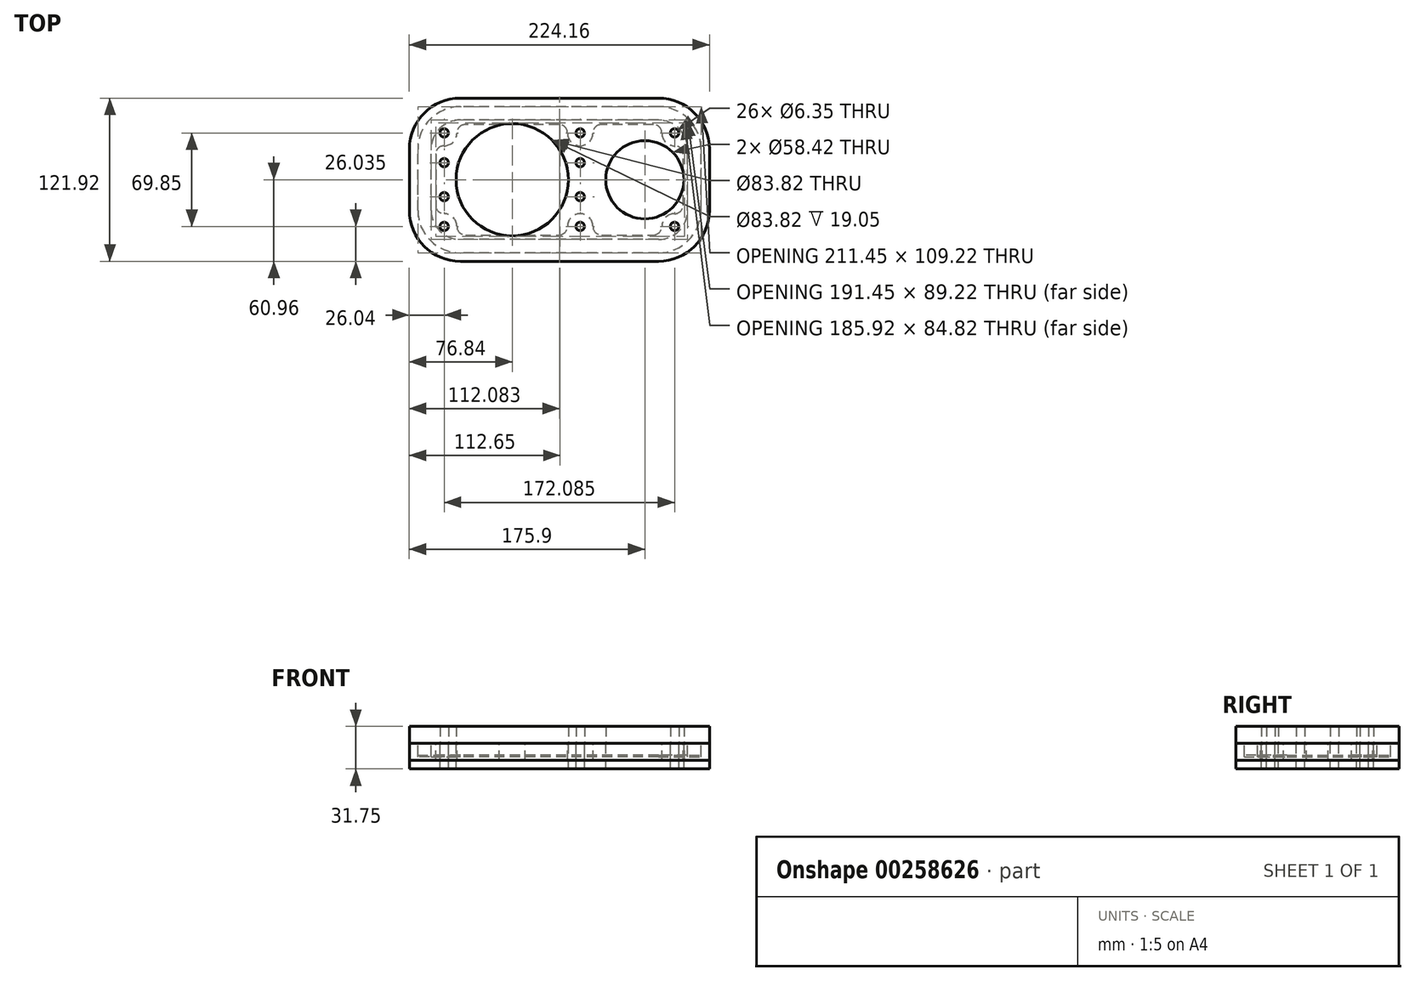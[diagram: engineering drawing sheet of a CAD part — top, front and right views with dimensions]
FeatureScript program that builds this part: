
annotation { "Feature Type Name" : "Feature", "Feature Type Description" : "" }
export const myFeature = defineFeature(function(context is Context, id is Id, definition is map)
    precondition{}
    {
        {
            var Q0;
            Q0=qCreatedBy(makeId("Top.planeOp"),FACE);
            var sketch = newSketch(context, id + "F0", { "sketchPlane" : qUnion([Q0])});
            skLineSegment(sketch, "E0.bottom", {"start": v(50.8, -12.7) * mm, "end": v(-50.8, -12.7) * mm, "construction": true});
            skLineSegment(sketch, "E0.top", {"start": v(50.8, 12.7) * mm, "end": v(-50.8, 12.7) * mm, "construction": true});
            skLineSegment(sketch, "E0.left", {"start": v(50.8, -12.7) * mm, "end": v(50.8, 12.7) * mm, "construction": true});
            skLineSegment(sketch, "E0.right", {"start": v(-50.8, -12.7) * mm, "end": v(-50.8, 12.7) * mm, "construction": true});
            skPoint(sketch, "E0.middle", {"position": v(0, 0) * mm});
            skCircle(sketch, "E1", {"center": v(0, 0) * mm, "radius": 41.91 * mm});
            skCircle(sketch, "E2", {"center": v(-50.8, 12.7) * mm, "radius": 3.18 * mm});
            skCircle(sketch, "E3", {"center": v(-50.8, -12.7) * mm, "radius": 3.18 * mm});
            skCircle(sketch, "E4", {"center": v(50.8, -12.7) * mm, "radius": 3.18 * mm});
            skCircle(sketch, "E5", {"center": v(50.8, 12.7) * mm, "radius": 3.18 * mm});
            skLineSegment(sketch, "E6.1", {"start": v(147.32, -22.86) * mm, "end": v(147.32, 22.86) * mm});
            skLineSegment(sketch, "E6.2", {"start": v(109.22, -60.96) * mm, "end": v(-38.74, -60.96) * mm});
            skLineSegment(sketch, "E6.5", {"start": v(-76.84, -22.86) * mm, "end": v(-76.84, 22.86) * mm});
            skLineSegment(sketch, "E6.7", {"start": v(109.22, 60.96) * mm, "end": v(-38.74, 60.96) * mm});
            skLineSegment(sketch, "E7", {"start": v(0, 0) * mm, "end": v(99.06, 0) * mm});
            skCircle(sketch, "E8", {"center": v(99.06, 0) * mm, "radius": 29.21 * mm});
            skPoint(sketch, "E9.visualSharp", {"position": v(-76.84, 60.96) * mm});
            skArc(sketch, "E9.filletArc", {"start": v(-38.74, 60.96) * mm, "mid": v(-65.68, 49.8) * mm, "end": v(-76.84, 22.86) * mm});
            skPoint(sketch, "E10.visualSharp", {"position": v(-76.84, -60.96) * mm});
            skArc(sketch, "E10.filletArc", {"start": v(-76.84, -22.86) * mm, "mid": v(-65.68, -49.8) * mm, "end": v(-38.74, -60.96) * mm});
            skPoint(sketch, "E11.visualSharp", {"position": v(147.32, -60.96) * mm});
            skArc(sketch, "E11.filletArc", {"start": v(109.22, -60.96) * mm, "mid": v(136.16, -49.8) * mm, "end": v(147.32, -22.86) * mm});
            skPoint(sketch, "E12.visualSharp", {"position": v(147.32, 60.96) * mm});
            skArc(sketch, "E12.filletArc", {"start": v(147.32, 22.86) * mm, "mid": v(136.16, 49.8) * mm, "end": v(109.22, 60.96) * mm});
            skArc(sketch, "E13.0", {"start": v(109.22, -54.61) * mm, "mid": v(131.67, -45.31) * mm, "end": v(140.97, -22.86) * mm});
            skLineSegment(sketch, "E13.1", {"start": v(140.97, -22.86) * mm, "end": v(140.97, 22.86) * mm});
            skLineSegment(sketch, "E13.2", {"start": v(109.22, -54.6) * mm, "end": v(-38.74, -54.61) * mm});
            skArc(sketch, "E13.3", {"start": v(140.97, 22.86) * mm, "mid": v(131.67, 45.31) * mm, "end": v(109.22, 54.61) * mm});
            skArc(sketch, "E13.4", {"start": v(-70.49, -22.86) * mm, "mid": v(-61.19, -45.31) * mm, "end": v(-38.74, -54.6) * mm});
            skLineSegment(sketch, "E13.5", {"start": v(-70.49, -22.86) * mm, "end": v(-70.49, 22.86) * mm});
            skArc(sketch, "E13.6", {"start": v(-38.74, 54.6) * mm, "mid": v(-61.19, 45.31) * mm, "end": v(-70.49, 22.86) * mm});
            skLineSegment(sketch, "E13.7", {"start": v(109.22, 54.61) * mm, "end": v(-38.74, 54.6) * mm});
            skArc(sketch, "E14.0", {"start": v(109.22, -44.61) * mm, "mid": v(124.6, -38.24) * mm, "end": v(130.97, -22.86) * mm});
            skLineSegment(sketch, "E14.1", {"start": v(130.97, -22.86) * mm, "end": v(130.97, 22.86) * mm});
            skLineSegment(sketch, "E14.2", {"start": v(109.22, -44.6) * mm, "end": v(-38.74, -44.61) * mm});
            skArc(sketch, "E14.3", {"start": v(130.97, 22.86) * mm, "mid": v(124.6, 38.24) * mm, "end": v(109.22, 44.61) * mm});
            skArc(sketch, "E14.4", {"start": v(-60.49, -22.86) * mm, "mid": v(-54.11, -38.24) * mm, "end": v(-38.74, -44.6) * mm});
            skLineSegment(sketch, "E14.5", {"start": v(-60.49, -22.86) * mm, "end": v(-60.49, 22.86) * mm});
            skArc(sketch, "E14.6", {"start": v(-38.74, 44.6) * mm, "mid": v(-54.11, 38.24) * mm, "end": v(-60.49, 22.86) * mm});
            skLineSegment(sketch, "E14.7", {"start": v(109.22, 44.61) * mm, "end": v(-38.74, 44.6) * mm});
            skCircle(sketch, "E15", {"center": v(-50.8, 34.93) * mm, "radius": 3.18 * mm});
            skCircle(sketch, "E16", {"center": v(50.8, 34.93) * mm, "radius": 3.18 * mm});
            skCircle(sketch, "E17", {"center": v(121.29, 34.93) * mm, "radius": 3.18 * mm});
            skCircle(sketch, "E18", {"center": v(121.29, -34.93) * mm, "radius": 3.18 * mm});
            skCircle(sketch, "E19", {"center": v(50.8, -34.93) * mm, "radius": 3.18 * mm});
            skCircle(sketch, "E20", {"center": v(-50.8, -34.93) * mm, "radius": 3.18 * mm});
            skLineSegment(sketch, "E21", {"start": v(0, 41.91) * mm, "end": v(0, 60.96) * mm, "construction": true});
            skLineSegment(sketch, "E22", {"start": v(128.27, 0) * mm, "end": v(147.32, 0) * mm, "construction": true});
            skLineSegment(sketch, "E23", {"start": v(0, -41.91) * mm, "end": v(0, -60.96) * mm, "construction": true});
            skPoint(sketch, "E24", {"position": v(41.91, 0) * mm});
            skPoint(sketch, "E25", {"position": v(69.85, 0) * mm});
            skSolve(sketch);
        }
        {
            var Q0;
            Q0=makeQuery(id+"F0.imprint","IMPRINT",FACE,{"disambiguationData":[TD([[makeQuery(id+"F0.imprint","IMPRINT",EDGE,{"derivedFrom":sQuery(id+"F0.wireOp",EDGE,"E1")}),-1.0]])]});
            var Q1;
            Q1=makeQuery(id+"F0.imprint","IMPRINT",FACE,{"disambiguationData":[TD([[makeQuery(id+"F0.imprint","IMPRINT",EDGE,{"derivedFrom":sQuery(id+"F0.wireOp",EDGE,"E13.0")}),1.0]])]});
            var Q2;
            Q2=makeQuery(id+"F0.imprint","IMPRINT",FACE,{"disambiguationData":[TD([[makeQuery(id+"F0.imprint","IMPRINT",EDGE,{"derivedFrom":sQuery(id+"F0.wireOp",EDGE,"E6.1")}),1.0]])]});
            extrude(context, id + "F1", {"entities" : qUnion([Q0, Q1, Q2]), "oppositeDirection" : true, "depth" : 19.05 * mm});
        }
        {
            var Q0;
            Q0=makeQuery(id+"F0.imprint","IMPRINT",FACE,{"disambiguationData":[TD([[makeQuery(id+"F0.imprint","IMPRINT",EDGE,{"derivedFrom":sQuery(id+"F0.wireOp",EDGE,"E13.0")}),1.0]])]});
            extrude(context, id + "F2", {"entities" : qUnion([Q0]), "operationType" : NewBodyOperationType.REMOVE, "oppositeDirection" : true, "depth" : 10 * mm});
        }
        {
            var Q0;
            Q0=qCreatedBy(makeId("Top.planeOp"),FACE);
            var sketch = newSketch(context, id + "F3", { "sketchPlane" : qUnion([Q0])});
            skPoint(sketch, "E26.0", {"position": v(-50.8, 34.93) * mm});
            skPoint(sketch, "E27.0", {"position": v(-50.8, -34.93) * mm});
            skPoint(sketch, "E28.0", {"position": v(-50.8, 12.7) * mm});
            skPoint(sketch, "E29.0", {"position": v(-50.8, -12.7) * mm});
            skPoint(sketch, "E30.0", {"position": v(0, 0) * mm});
            skPoint(sketch, "E31.0", {"position": v(50.8, 34.93) * mm});
            skPoint(sketch, "E32.0", {"position": v(50.8, 12.7) * mm});
            skPoint(sketch, "E33.0", {"position": v(50.8, -12.7) * mm});
            skPoint(sketch, "E34.0", {"position": v(50.8, -34.93) * mm});
            skPoint(sketch, "E35.0", {"position": v(99.06, 0) * mm});
            skPoint(sketch, "E36.0", {"position": v(121.29, 34.93) * mm});
            skPoint(sketch, "E37.0", {"position": v(121.29, -34.93) * mm});
            skPoint(sketch, "E38.0", {"position": v(109.22, -22.86) * mm});
            skPoint(sketch, "E39.0", {"position": v(109.22, -60.96) * mm});
            skPoint(sketch, "E40.0", {"position": v(147.32, -22.86) * mm});
            skPoint(sketch, "E41.0", {"position": v(147.32, 22.86) * mm});
            skPoint(sketch, "E42.0", {"position": v(109.22, 60.96) * mm});
            skPoint(sketch, "E43.0", {"position": v(-38.74, 60.96) * mm});
            skPoint(sketch, "E44.0", {"position": v(-76.84, 22.86) * mm});
            skPoint(sketch, "E45.0", {"position": v(-76.84, -22.86) * mm});
            skPoint(sketch, "E46.0", {"position": v(-38.74, -60.96) * mm});
            skPoint(sketch, "E47.0", {"position": v(-38.74, 22.86) * mm});
            skPoint(sketch, "E48.0", {"position": v(-38.74, -22.86) * mm});
            skArc(sketch, "E49", {"start": v(-38.74, 60.96) * mm, "mid": v(-65.68, 49.8) * mm, "end": v(-76.84, 22.86) * mm});
            skArc(sketch, "E50", {"start": v(-76.84, -22.86) * mm, "mid": v(-65.68, -49.8) * mm, "end": v(-38.74, -60.96) * mm});
            skArc(sketch, "E51", {"start": v(109.22, -60.96) * mm, "mid": v(136.16, -49.8) * mm, "end": v(147.32, -22.86) * mm});
            skPoint(sketch, "E52.0", {"position": v(109.22, 22.86) * mm});
            skArc(sketch, "E53", {"start": v(147.32, 22.86) * mm, "mid": v(136.16, 49.8) * mm, "end": v(109.22, 60.96) * mm});
            skLineSegment(sketch, "E54", {"start": v(-38.74, 60.96) * mm, "end": v(109.22, 60.96) * mm});
            skLineSegment(sketch, "E55", {"start": v(147.32, 22.86) * mm, "end": v(147.32, -22.86) * mm});
            skLineSegment(sketch, "E56", {"start": v(109.22, -60.96) * mm, "end": v(-38.74, -60.96) * mm});
            skLineSegment(sketch, "E57", {"start": v(-76.84, -22.86) * mm, "end": v(-76.84, 22.86) * mm});
            skPoint(sketch, "E58.0", {"position": v(41.91, 0) * mm});
            skPoint(sketch, "E59.0", {"position": v(69.85, 0) * mm});
            skCircle(sketch, "E60", {"center": v(0, 0) * mm, "radius": 41.91 * mm});
            skCircle(sketch, "E61", {"center": v(99.06, 0) * mm, "radius": 29.21 * mm});
            skCircle(sketch, "E62", {"center": v(-50.8, 34.93) * mm, "radius": 3.18 * mm});
            skCircle(sketch, "E63", {"center": v(-50.8, 12.7) * mm, "radius": 3.18 * mm});
            skCircle(sketch, "E64", {"center": v(-50.8, -12.7) * mm, "radius": 3.17 * mm});
            skCircle(sketch, "E65", {"center": v(-50.8, -34.93) * mm, "radius": 3.17 * mm});
            skCircle(sketch, "E66", {"center": v(50.8, -34.93) * mm, "radius": 3.18 * mm});
            skCircle(sketch, "E67", {"center": v(50.8, -12.7) * mm, "radius": 3.18 * mm});
            skCircle(sketch, "E68", {"center": v(50.8, 12.7) * mm, "radius": 3.18 * mm});
            skCircle(sketch, "E69", {"center": v(50.8, 34.93) * mm, "radius": 3.18 * mm});
            skCircle(sketch, "E70", {"center": v(121.29, 34.93) * mm, "radius": 3.18 * mm});
            skCircle(sketch, "E71", {"center": v(121.29, -34.93) * mm, "radius": 3.18 * mm});
            skSolve(sketch);
        }
        {
            var Q0;
            Q0=qCreatedBy(makeId("Top.planeOp"),FACE);
            var sketch = newSketch(context, id + "F4", { "sketchPlane" : qUnion([Q0])});
            skPoint(sketch, "E72.0", {"position": v(-38.74, 22.86) * mm});
            skPoint(sketch, "E73.0", {"position": v(-38.74, -22.86) * mm});
            skPoint(sketch, "E74.0", {"position": v(-38.74, -60.96) * mm});
            skPoint(sketch, "E75.0", {"position": v(-38.74, -54.61) * mm});
            skPoint(sketch, "E76.0", {"position": v(-38.74, -44.61) * mm});
            skPoint(sketch, "E77.0", {"position": v(-60.49, -22.86) * mm});
            skPoint(sketch, "E78.0", {"position": v(-70.49, -22.86) * mm});
            skPoint(sketch, "E79.0", {"position": v(-76.84, -22.86) * mm});
            skPoint(sketch, "E80.0", {"position": v(-76.84, 22.86) * mm});
            skPoint(sketch, "E81.0", {"position": v(-70.49, 22.86) * mm});
            skPoint(sketch, "E82.0", {"position": v(-60.49, 22.86) * mm});
            skPoint(sketch, "E83.0", {"position": v(-38.74, 44.6) * mm});
            skPoint(sketch, "E84.0", {"position": v(-38.74, 54.6) * mm});
            skPoint(sketch, "E85.0", {"position": v(-38.74, 60.96) * mm});
            skPoint(sketch, "E86.0", {"position": v(109.22, 60.96) * mm});
            skPoint(sketch, "E87.0", {"position": v(109.22, 54.61) * mm});
            skPoint(sketch, "E88.0", {"position": v(109.22, 44.61) * mm});
            skPoint(sketch, "E89.0", {"position": v(109.22, 22.86) * mm});
            skPoint(sketch, "E90.0", {"position": v(130.97, 22.86) * mm});
            skPoint(sketch, "E91.0", {"position": v(140.97, 22.86) * mm});
            skPoint(sketch, "E92.0", {"position": v(147.32, 22.86) * mm});
            skPoint(sketch, "E93.0", {"position": v(147.32, -22.86) * mm});
            skPoint(sketch, "E94.0", {"position": v(140.97, -22.86) * mm});
            skPoint(sketch, "E95.0", {"position": v(130.97, -22.86) * mm});
            skPoint(sketch, "E96.0", {"position": v(109.22, -44.6) * mm});
            skPoint(sketch, "E97.0", {"position": v(109.22, -54.6) * mm});
            skPoint(sketch, "E98.0", {"position": v(109.22, -60.96) * mm});
            skPoint(sketch, "E99.0", {"position": v(-50.8, 34.93) * mm});
            skPoint(sketch, "E100.0", {"position": v(-50.8, -34.93) * mm});
            skPoint(sketch, "E101.0", {"position": v(50.8, -34.93) * mm});
            skPoint(sketch, "E102.0", {"position": v(50.8, 34.93) * mm});
            skPoint(sketch, "E103.0", {"position": v(121.29, 34.93) * mm});
            skPoint(sketch, "E104.0", {"position": v(121.29, -34.93) * mm});
            skArc(sketch, "E105", {"start": v(-38.74, 44.6) * mm, "mid": v(-54.11, 38.24) * mm, "end": v(-60.49, 22.86) * mm});
            skArc(sketch, "E106", {"start": v(-38.74, 54.61) * mm, "mid": v(-61.19, 45.31) * mm, "end": v(-70.49, 22.86) * mm});
            skArc(sketch, "E107", {"start": v(-38.74, 60.96) * mm, "mid": v(-65.68, 49.8) * mm, "end": v(-76.84, 22.86) * mm});
            skArc(sketch, "E108", {"start": v(-60.49, -22.86) * mm, "mid": v(-54.11, -38.24) * mm, "end": v(-38.74, -44.6) * mm});
            skArc(sketch, "E109", {"start": v(-70.48, -22.86) * mm, "mid": v(-61.19, -45.31) * mm, "end": v(-38.74, -54.6) * mm});
            skArc(sketch, "E110", {"start": v(-76.84, -22.86) * mm, "mid": v(-65.68, -49.8) * mm, "end": v(-38.74, -60.96) * mm});
            skPoint(sketch, "E111.0", {"position": v(109.22, -22.86) * mm});
            skArc(sketch, "E112", {"start": v(130.97, -22.86) * mm, "mid": v(124.6, -38.24) * mm, "end": v(109.22, -44.61) * mm});
            skArc(sketch, "E113", {"start": v(140.97, -22.86) * mm, "mid": v(131.67, -45.31) * mm, "end": v(109.22, -54.61) * mm});
            skArc(sketch, "E114", {"start": v(147.32, -22.86) * mm, "mid": v(136.16, -49.8) * mm, "end": v(109.22, -60.96) * mm});
            skArc(sketch, "E115", {"start": v(130.97, 22.86) * mm, "mid": v(124.6, 38.24) * mm, "end": v(109.22, 44.61) * mm});
            skArc(sketch, "E116", {"start": v(140.97, 22.86) * mm, "mid": v(131.67, 45.31) * mm, "end": v(109.22, 54.61) * mm});
            skArc(sketch, "E117", {"start": v(147.32, 22.86) * mm, "mid": v(136.16, 49.8) * mm, "end": v(109.22, 60.96) * mm});
            skLineSegment(sketch, "E118", {"start": v(109.22, 44.61) * mm, "end": v(-38.74, 44.6) * mm});
            skLineSegment(sketch, "E119", {"start": v(-38.74, 54.6) * mm, "end": v(109.22, 54.61) * mm});
            skLineSegment(sketch, "E120", {"start": v(109.22, 60.96) * mm, "end": v(-38.74, 60.96) * mm});
            skLineSegment(sketch, "E121", {"start": v(-60.49, 22.86) * mm, "end": v(-60.49, -22.86) * mm});
            skLineSegment(sketch, "E122", {"start": v(-70.49, -22.86) * mm, "end": v(-70.49, 22.86) * mm});
            skLineSegment(sketch, "E123", {"start": v(-76.84, 22.86) * mm, "end": v(-76.84, -22.86) * mm});
            skLineSegment(sketch, "E124", {"start": v(-38.74, -44.61) * mm, "end": v(109.22, -44.6) * mm});
            skLineSegment(sketch, "E125", {"start": v(109.22, -54.6) * mm, "end": v(-38.74, -54.6) * mm});
            skLineSegment(sketch, "E126", {"start": v(-38.74, -60.96) * mm, "end": v(109.22, -60.96) * mm});
            skLineSegment(sketch, "E127", {"start": v(130.97, -22.86) * mm, "end": v(130.97, 22.86) * mm});
            skLineSegment(sketch, "E128", {"start": v(140.97, -22.86) * mm, "end": v(140.97, 22.86) * mm});
            skLineSegment(sketch, "E129", {"start": v(147.32, -22.86) * mm, "end": v(147.32, 22.86) * mm});
            skPoint(sketch, "E130.0", {"position": v(-50.8, -12.7) * mm});
            skPoint(sketch, "E131.0", {"position": v(-50.8, 12.7) * mm});
            skPoint(sketch, "E132.0", {"position": v(50.8, -12.7) * mm});
            skPoint(sketch, "E133.0", {"position": v(50.8, 12.7) * mm});
            skArc(sketch, "E134", {"start": v(-50.8, 25.4) * mm, "mid": v(-44.06, 28.19) * mm, "end": v(-41.28, 34.93) * mm});
            skArc(sketch, "E135", {"start": v(-50.8, 25.4) * mm, "mid": v(-55.3, 23.54) * mm, "end": v(-57.15, 19.05) * mm});
            skArc(sketch, "E136", {"start": v(-41.28, -34.93) * mm, "mid": v(-44.06, -28.19) * mm, "end": v(-50.8, -25.4) * mm});
            skArc(sketch, "E137", {"start": v(-41.28, -34.93) * mm, "mid": v(-39.42, -39.42) * mm, "end": v(-34.93, -41.28) * mm});
            skArc(sketch, "E138", {"start": v(34.93, -41.28) * mm, "mid": v(39.42, -39.42) * mm, "end": v(41.28, -34.93) * mm});
            skArc(sketch, "E139", {"start": v(60.33, -34.93) * mm, "mid": v(50.8, -25.4) * mm, "end": v(41.28, -34.93) * mm});
            skArc(sketch, "E140", {"start": v(60.33, -34.93) * mm, "mid": v(62.18, -39.42) * mm, "end": v(66.68, -41.28) * mm});
            skArc(sketch, "E141", {"start": v(105.41, -41.27) * mm, "mid": v(109.9, -39.42) * mm, "end": v(111.76, -34.92) * mm});
            skArc(sketch, "E142", {"start": v(121.29, -25.4) * mm, "mid": v(114.55, -28.19) * mm, "end": v(111.76, -34.92) * mm});
            skArc(sketch, "E143", {"start": v(121.29, -25.4) * mm, "mid": v(125.78, -23.54) * mm, "end": v(127.64, -19.05) * mm});
            skArc(sketch, "E144", {"start": v(127.64, 19.05) * mm, "mid": v(125.78, 23.54) * mm, "end": v(121.29, 25.4) * mm});
            skArc(sketch, "E145", {"start": v(111.76, 34.93) * mm, "mid": v(114.55, 28.19) * mm, "end": v(121.29, 25.4) * mm});
            skArc(sketch, "E146", {"start": v(111.76, 34.93) * mm, "mid": v(109.9, 39.42) * mm, "end": v(105.41, 41.28) * mm});
            skArc(sketch, "E147", {"start": v(66.68, 41.28) * mm, "mid": v(62.18, 39.42) * mm, "end": v(60.33, 34.93) * mm});
            skArc(sketch, "E148", {"start": v(-34.93, 41.28) * mm, "mid": v(-39.42, 39.42) * mm, "end": v(-41.28, 34.93) * mm});
            skArc(sketch, "E149", {"start": v(41.28, 34.93) * mm, "mid": v(50.8, 25.4) * mm, "end": v(60.33, 34.93) * mm});
            skArc(sketch, "E150", {"start": v(41.28, 34.93) * mm, "mid": v(39.42, 39.42) * mm, "end": v(34.93, 41.28) * mm});
            skArc(sketch, "E151", {"start": v(-57.15, -19.05) * mm, "mid": v(-55.3, -23.54) * mm, "end": v(-50.8, -25.4) * mm});
            skLineSegment(sketch, "E152", {"start": v(-57.15, 19.05) * mm, "end": v(-57.15, -19.05) * mm});
            skLineSegment(sketch, "E153", {"start": v(-34.93, -41.28) * mm, "end": v(-9.75, -41.28) * mm});
            skLineSegment(sketch, "E154", {"start": v(66.68, -41.28) * mm, "end": v(105.41, -41.28) * mm});
            skLineSegment(sketch, "E155", {"start": v(127.64, -19.05) * mm, "end": v(127.64, -8.13) * mm});
            skLineSegment(sketch, "E156", {"start": v(105.41, 41.28) * mm, "end": v(66.68, 41.28) * mm});
            skLineSegment(sketch, "E157", {"start": v(34.93, 41.28) * mm, "end": v(9.75, 41.28) * mm});
            skCircle(sketch, "E158", {"center": v(-50.8, 34.93) * mm, "radius": 3.18 * mm});
            skCircle(sketch, "E159", {"center": v(-50.8, -34.93) * mm, "radius": 3.18 * mm});
            skCircle(sketch, "E160", {"center": v(50.8, -34.93) * mm, "radius": 3.18 * mm});
            skCircle(sketch, "E161", {"center": v(50.8, 34.93) * mm, "radius": 3.18 * mm});
            skCircle(sketch, "E162", {"center": v(121.29, 34.93) * mm, "radius": 3.18 * mm});
            skCircle(sketch, "E163", {"center": v(121.29, -34.93) * mm, "radius": 3.18 * mm});
            skCircle(sketch, "E164.0", {"center": v(99.06, 0) * mm, "radius": 29.21 * mm});
            skPoint(sketch, "E165.0", {"position": v(0, 0) * mm});
            skCircle(sketch, "E166.0", {"center": v(0, 0) * mm, "radius": 41.91 * mm});
            skArc(sketch, "E167", {"start": v(-9.75, -41.28) * mm, "mid": v(0, -42.41) * mm, "end": v(9.75, -41.28) * mm});
            skArc(sketch, "E168", {"start": v(127.64, -8.13) * mm, "mid": v(128.77, 0) * mm, "end": v(127.64, 8.13) * mm});
            skArc(sketch, "E169.trimOffspring", {"start": v(9.75, 41.28) * mm, "mid": v(0, 42.41) * mm, "end": v(-9.75, 41.28) * mm});
            skLineSegment(sketch, "E170", {"start": v(-9.75, 41.28) * mm, "end": v(-34.93, 41.28) * mm});
            skLineSegment(sketch, "E171", {"start": v(9.75, 41.28) * mm, "end": v(-9.75, 41.28) * mm, "construction": true});
            skLineSegment(sketch, "E172", {"start": v(-9.75, -41.28) * mm, "end": v(9.75, -41.28) * mm, "construction": true});
            skLineSegment(sketch, "E173", {"start": v(9.75, -41.28) * mm, "end": v(34.93, -41.28) * mm});
            skLineSegment(sketch, "E174", {"start": v(127.64, 8.13) * mm, "end": v(127.64, 19.05) * mm});
            skLineSegment(sketch, "E175", {"start": v(127.64, -8.13) * mm, "end": v(127.64, 8.13) * mm, "construction": true});
            skSolve(sketch);
        }
        {
            var Q0;
            Q0 = qSketchRegion(id + "F3", true);
            extrude(context, id + "F5", {"entities" : qUnion([Q0]), "depth" : 12.7 * mm});
        }
        {
            var Q0;
            Q0 = qSketchRegion(id + "F4", true);
            var Q1;
            Q1=makeQuery(id+"F4.imprint","IMPRINT",FACE,{"disambiguationData":[TD([[makeQuery(id+"F4.imprint","IMPRINT",EDGE,{"derivedFrom":sQuery(id+"F4.wireOp",EDGE,"E105")}),-1.0]])]});
            var Q2;
            Q2=makeQuery(id+"F4.imprint","IMPRINT",FACE,{"disambiguationData":[TD([[makeQuery(id+"F4.imprint","IMPRINT",EDGE,{"derivedFrom":sQuery(id+"F4.wireOp",EDGE,"E105")}),1.0]])]});
            extrude(context, id + "F6", {"entities" : qUnion([Q0, Q1, Q2]), "oppositeDirection" : true, "depth" : 12.7 * mm});
        }
        {
            var Q0;
            Q0=makeQuery(id+"F4.imprint","IMPRINT",FACE,{"disambiguationData":[TD([[makeQuery(id+"F4.imprint","IMPRINT",EDGE,{"derivedFrom":sQuery(id+"F4.wireOp",EDGE,"E105")}),-1.0]])]});
            extrude(context, id + "F7", {"entities" : qUnion([Q0]), "operationType" : NewBodyOperationType.REMOVE, "oppositeDirection" : true, "depth" : 8.9 * mm});
        }
    });
